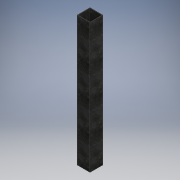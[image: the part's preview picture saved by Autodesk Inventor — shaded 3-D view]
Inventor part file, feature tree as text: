
AUTODESK INVENTOR PART (.ipt)
format: ipt  version: 2017 (Build 210142000, 142)  size: 108,032 bytes
history: native  units: mm
features: other x1, extrude x1, sketch x1
ambient origin geometry x8: Origin, YZ Plane, XZ Plane, XY Plane, X Axis, Y Axis, Z Axis, Center Point
bodies: Body1 (feature_tree)
feature tree (3):
  other  "Sólido1"
  extrude  "Extrusión1"  Depth=75.0mm
  sketch  "Boceto1"  dims[d0=75.0mm d1=75.0mm d2=3.0mm d3=37.5mm d4=37.5mm d5=750.0mm d6=0.0mm]
